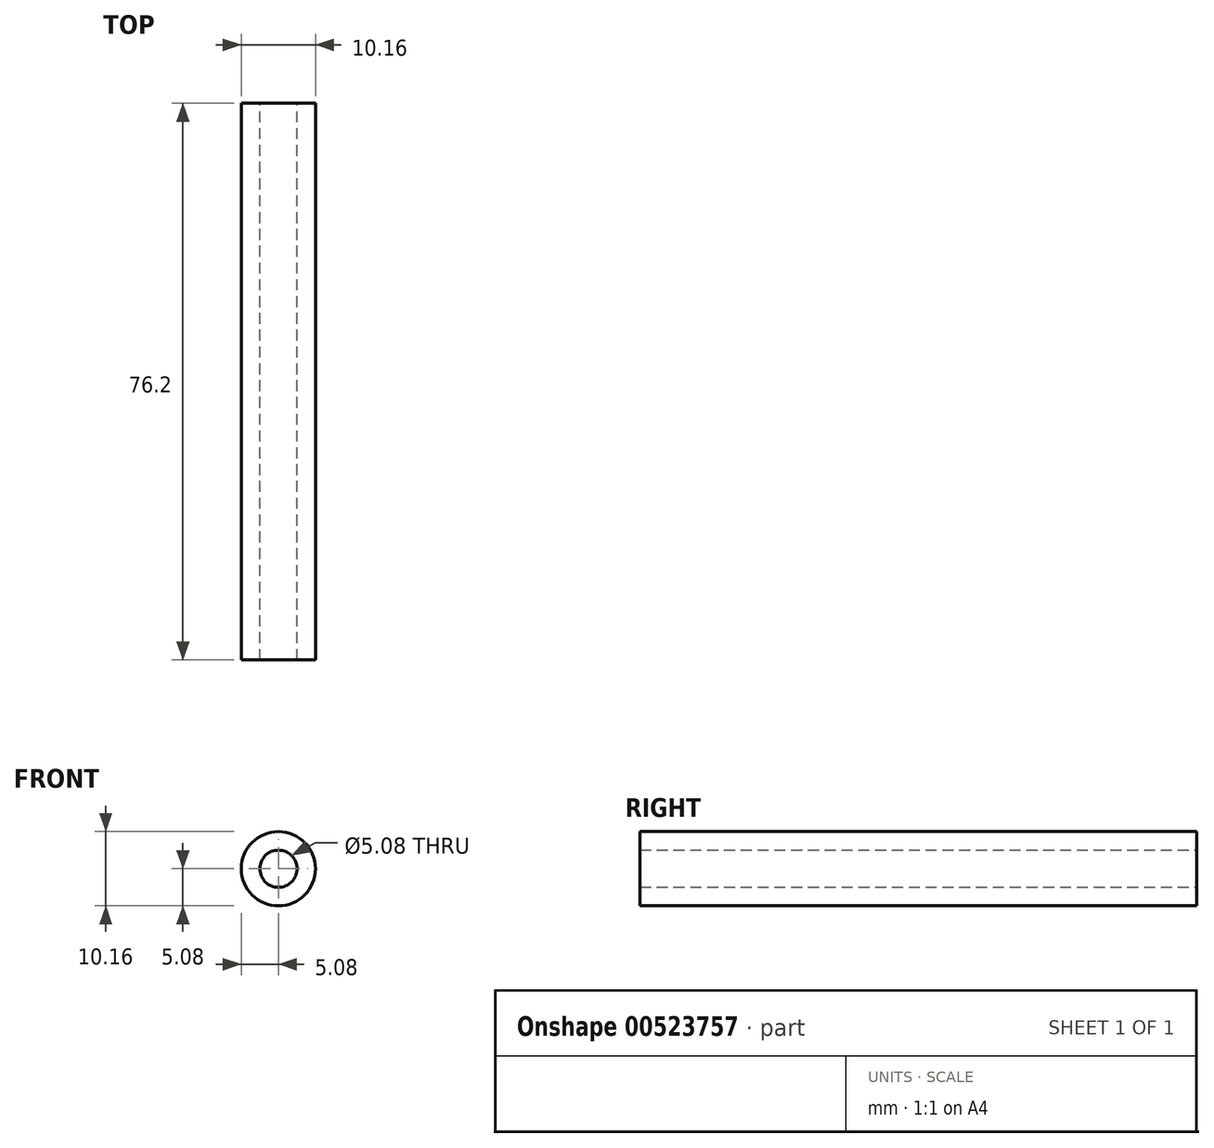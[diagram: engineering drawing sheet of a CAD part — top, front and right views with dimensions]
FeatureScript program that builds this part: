
annotation { "Feature Type Name" : "Feature", "Feature Type Description" : "" }
export const myFeature = defineFeature(function(context is Context, id is Id, definition is map)
    precondition{}
    {
        {
            var Q0;
            Q0=qCreatedBy(makeId("Front.planeOp"),FACE);
            var sketch = newSketch(context, id + "F0", { "sketchPlane" : qUnion([Q0])});
            skCircle(sketch, "E0", {"center": v(0, 0) * mm, "radius": 5.08 * mm});
            skCircle(sketch, "E1", {"center": v(0, 0) * mm, "radius": 2.54 * mm});
            skSolve(sketch);
        }
        {
            var Q0;
            Q0=makeQuery(id+"F0.imprint","IMPRINT",FACE,{"disambiguationData":[TD([[makeQuery(id+"F0.imprint","IMPRINT",EDGE,{"derivedFrom":sQuery(id+"F0.wireOp",EDGE,"E0")}),1.0]])]});
            extrude(context, id + "F1", {"entities" : qUnion([Q0]), "depth" : 76.2 * mm, "offsetDistance" : 25.4 * mm});
        }
    });
